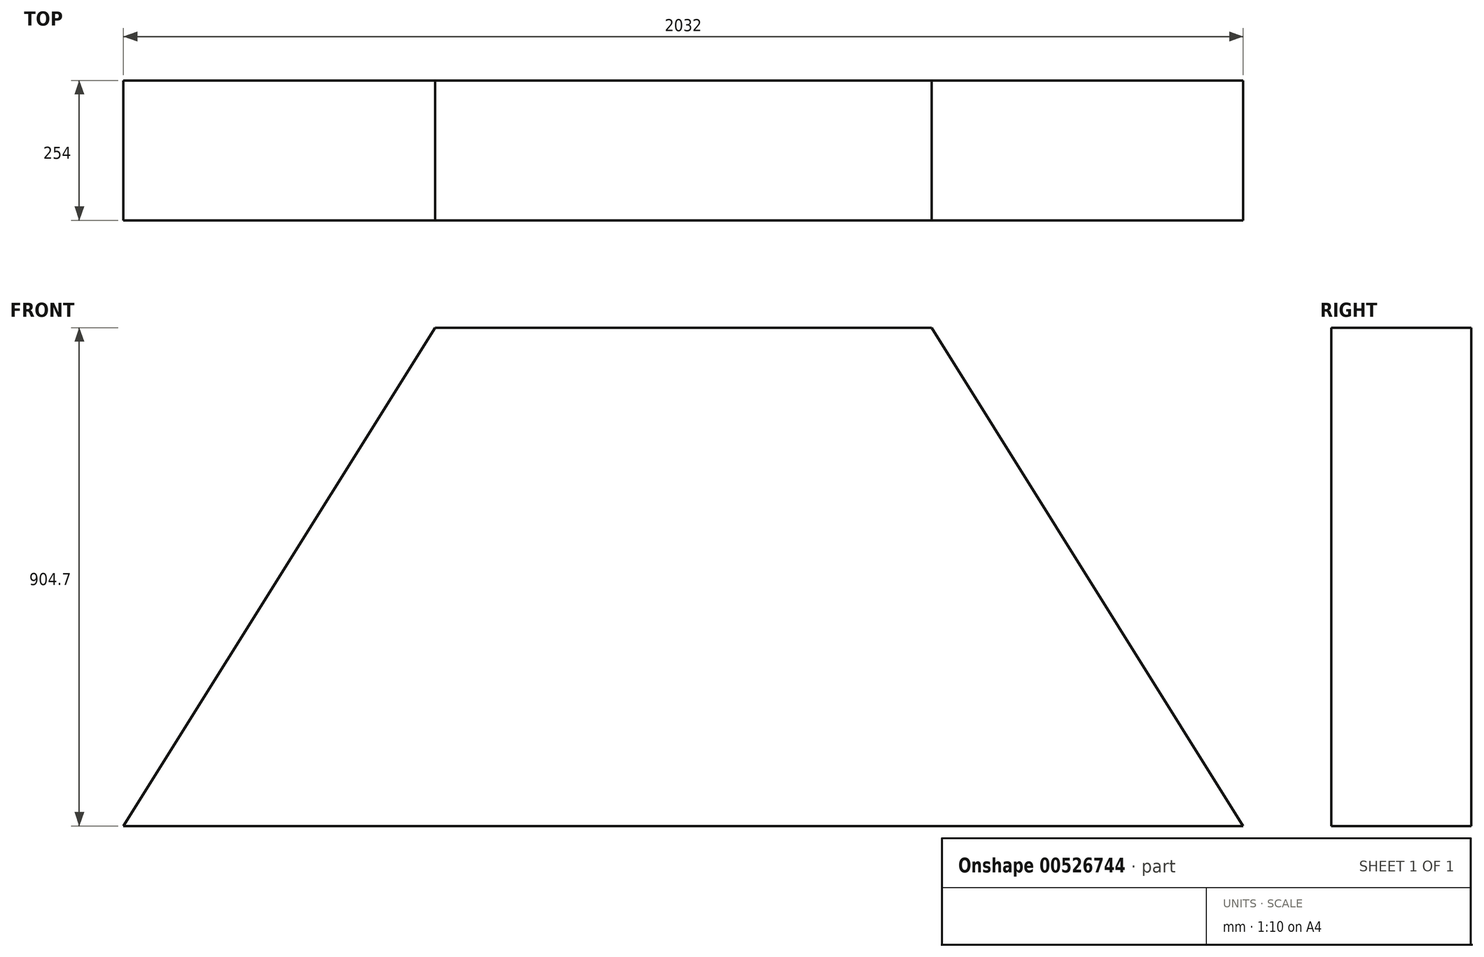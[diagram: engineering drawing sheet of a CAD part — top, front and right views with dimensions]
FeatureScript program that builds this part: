
annotation { "Feature Type Name" : "Feature", "Feature Type Description" : "" }
export const myFeature = defineFeature(function(context is Context, id is Id, definition is map)
    precondition{}
    {
        {
            var Q0;
            Q0=qCreatedBy(makeId("Front.planeOp"),FACE);
            var sketch = newSketch(context, id + "F0", { "sketchPlane" : qUnion([Q0])});
            skLineSegment(sketch, "E0", {"start": v(0, 0) * mm, "end": v(2032, 0) * mm});
            skLineSegment(sketch, "E1", {"start": v(2032, 0) * mm, "end": v(1466.68, 904.7) * mm});
            skLineSegment(sketch, "E2", {"start": v(0, 0) * mm, "end": v(565.32, 904.7) * mm});
            skLineSegment(sketch, "E3", {"start": v(565.32, 904.7) * mm, "end": v(1466.68, 904.7) * mm});
            skSolve(sketch);
        }
        {
            var Q0;
            Q0 = qSketchRegion(id + "F0", true);
            extrude(context, id + "F1", {"entities" : qUnion([Q0]), "depth" : 254 * mm, "offsetDistance" : 25.4 * mm});
        }
    });
